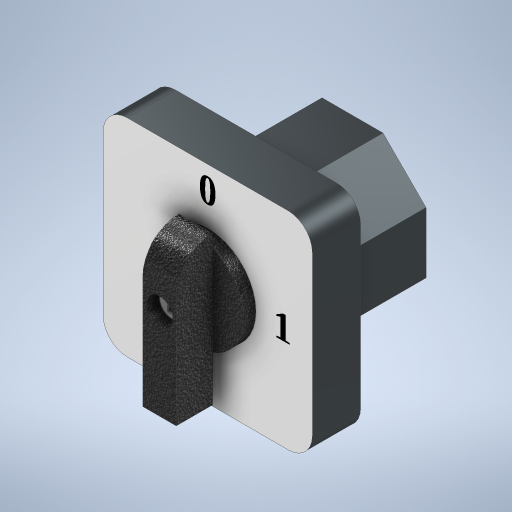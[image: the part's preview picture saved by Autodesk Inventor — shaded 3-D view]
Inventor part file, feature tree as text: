
AUTODESK INVENTOR PART (.ipt)
format: ipt  version: 2023 (Build 270158000, 158)  size: 407,040 bytes
history: native  units: in
note: dims shown in document units (in); Inventor stores cm internally (conversion verified against a paired STEP export)
features: sketch x10, other x8, extrude x7, fillet x2
ambient origin geometry x8: Origin, YZ Plane, XZ Plane, XY Plane, X Axis, Y Axis, Z Axis, Center Point
bodies: Solid1 (feature_tree)
feature tree (27):
  extrude  "Extrusion1"  Depth=0.7874in TaperAngle=0.0deg
  extrude  "Extrusion2"  Depth=0.1969in TaperAngle=0.0deg
  fillet  "Fillet1"  Radius=0.5906in
  extrude  "Extrusion3"  Depth=0.7874in TaperAngle=0.0deg
  extrude  "Extrusion4"  Depth=0.5906in TaperAngle=0.0deg
  fillet  "Fillet2"  Radius=0.1969in
  extrude  "Extrusion5"  Depth=2.4in
  extrude  "Extrusion6"  [1 undecoded]
  extrude  "Extrusion7"  [1 undecoded]
  sketch  "Sketch8"
  other  "Decal1"
  other  "Decal2"
  sketch  "Sketch9"
  sketch  "Sketch10"
  other  "Decal3"
  other  "Decal4"
  sketch  "Sketch1"  dims[d1=1.5748in d2=0.0in d3=0.7874in d4=0.0in]
  sketch  "Sketch2"  dims[d5=0.3937in d6=0.1969in d7=0.0in d8=0.5906in d9=0.0in]
  sketch  "Sketch3"  dims[d10=0.5906in d11=0.7874in d12=0.0in]
  sketch  "Sketch4"  dims[d13=0.4in d14=0.5906in d15=0.0in d16=0.1969in d17=0.0in]
  sketch  "Sketch5"  dims[d50=2.4in d54=1.2in]
  sketch  "Sketch6"
  sketch  "Sketch7"
  other  "Image1"
  other  "Image2"
  other  "Image4"
  other  "Image5"
note: 2 required parameter values undecoded (feature->parameter linkage not recoverable at this tier; creation-order binding heuristic only, values carry confidence <= 0.55)
